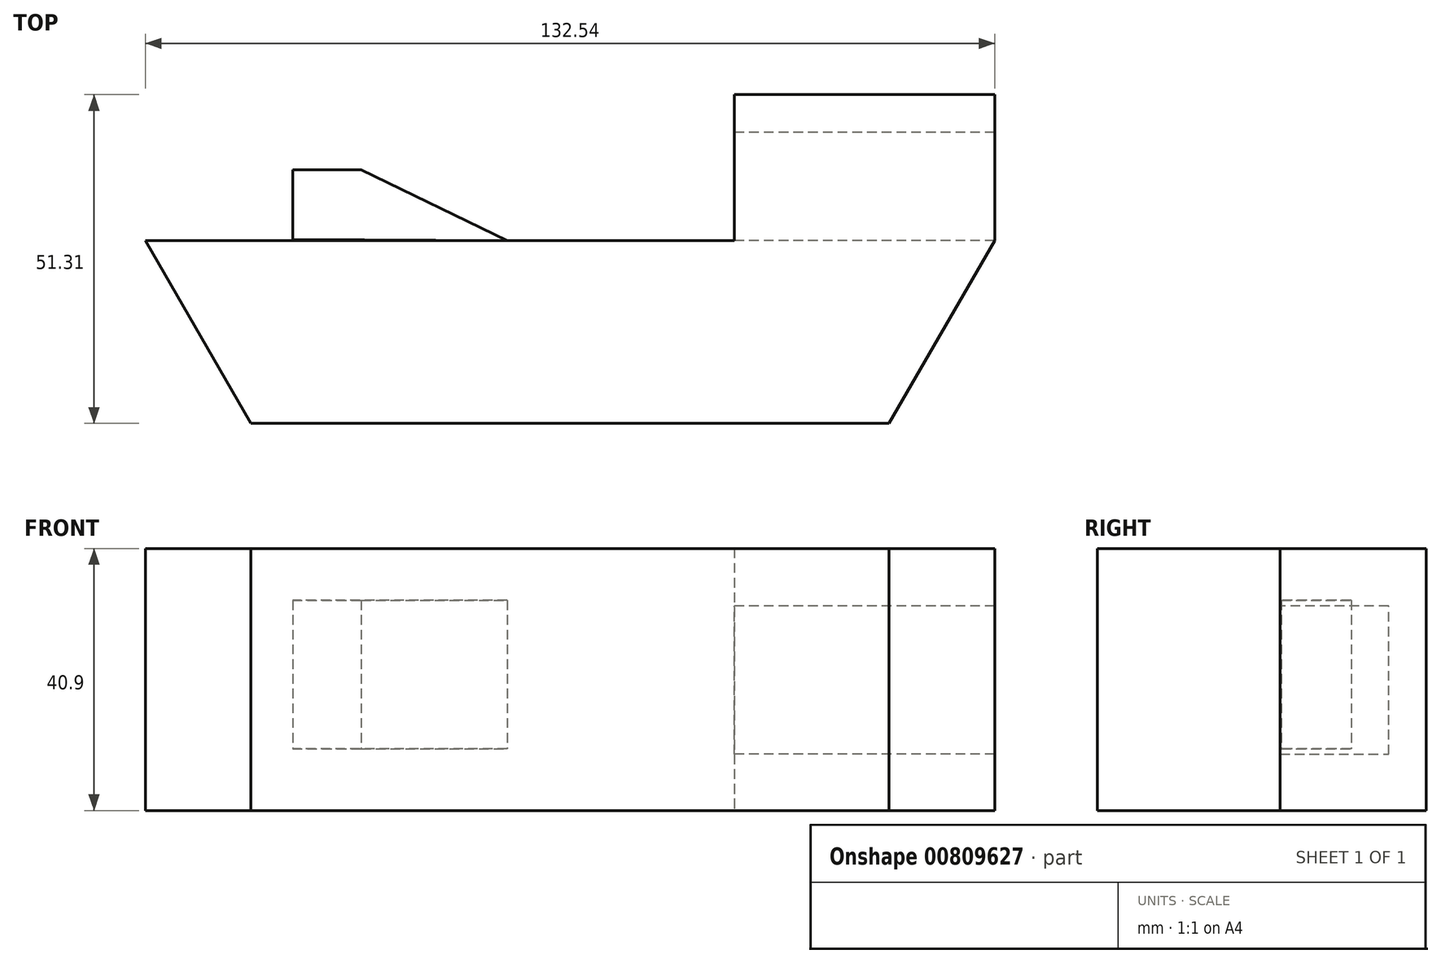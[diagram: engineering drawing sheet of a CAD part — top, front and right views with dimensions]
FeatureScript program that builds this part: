
annotation { "Feature Type Name" : "Feature", "Feature Type Description" : "" }
export const myFeature = defineFeature(function(context is Context, id is Id, definition is map)
    precondition{}
    {
        {
            var Q0;
            Q0=qCreatedBy(makeId("Top.planeOp"),FACE);
            var sketch = newSketch(context, id + "F0", { "sketchPlane" : qUnion([Q0])});
            skLineSegment(sketch, "E0.bottom", {"start": v(-66.27, 14.26) * mm, "end": v(66.27, 14.26) * mm});
            skLineSegment(sketch, "E0.top", {"start": v(-49.8, -14.26) * mm, "end": v(49.8, -14.26) * mm});
            skPoint(sketch, "E0.middle", {"position": v(0, 0) * mm});
            skLineSegment(sketch, "E1", {"start": v(-66.27, 14.26) * mm, "end": v(-49.8, -14.26) * mm});
            skLineSegment(sketch, "E2", {"start": v(66.27, 14.26) * mm, "end": v(49.8, -14.26) * mm});
            skPoint(sketch, "E3.orphan", {"position": v(-66.27, -14.26) * mm});
            skPoint(sketch, "E4.orphan", {"position": v(66.27, -14.26) * mm});
            skLineSegment(sketch, "E5", {"start": v(66.27, 14.26) * mm, "end": v(66.27, 37.05) * mm});
            skLineSegment(sketch, "E6", {"start": v(66.27, 37.05) * mm, "end": v(25.66, 37.05) * mm});
            skLineSegment(sketch, "E7", {"start": v(25.66, 37.05) * mm, "end": v(25.66, 14.26) * mm});
            skLineSegment(sketch, "E8", {"start": v(25.66, 14.26) * mm, "end": v(66.27, 14.26) * mm});
            skSolve(sketch);
        }
        {
            var Q0;
            Q0 = qSketchRegion(id + "F0", true);
            extrude(context, id + "F1", {"entities" : qUnion([Q0]), "depth" : 40.9 * mm, "offsetDistance" : 25 * mm});
        }
        {
            var Q0;
            Q0=qCreatedBy(makeId("Top.planeOp"),FACE);
            cPlane(context, id + "F2", {"entities" : qUnion([Q0]), "cplaneType" : CPlaneType.OFFSET, "offset" : 21.2 * mm, "width" : 150 * mm, "height" : 150 * mm});
        }
        {
            var Q0;
            Q0=qCreatedBy(id+"F2.planeOp",FACE);
            var sketch = newSketch(context, id + "F3", { "sketchPlane" : qUnion([Q0])});
            skLineSegment(sketch, "E9", {"start": v(-43.29, 14.46) * mm, "end": v(-43.29, 25.36) * mm});
            skLineSegment(sketch, "E10", {"start": v(-43.29, 25.36) * mm, "end": v(-32.59, 25.36) * mm});
            skLineSegment(sketch, "E11", {"start": v(-32.59, 25.36) * mm, "end": v(-9.8, 14.26) * mm});
            skLineSegment(sketch, "E12", {"start": v(-9.8, 14.26) * mm, "end": v(-43.29, 14.46) * mm});
            skSolve(sketch);
        }
        {
            var Q0;
            Q0=makeQuery(id+"F3.imprint","IMPRINT",FACE,{"disambiguationData":[TD([[makeQuery(id+"F3.imprint","IMPRINT",EDGE,{"derivedFrom":sQuery(id+"F3.wireOp",EDGE,"E9")}),-1.0]])]});
            extrude(context, id + "F4", {"entities" : qUnion([Q0]), "endBound" : BoundingType.SYMMETRIC, "depth" : 23.2 * mm, "offsetDistance" : 25 * mm});
        }
        {
            var Q0;
            Q0=makeQuery(id+"F1.opExtrude","SWEPT_FACE",FACE,{"disambiguationData":[OSD([sQuery(id+"F0.wireOp",EDGE,"E7")])]});
            var sketch = newSketch(context, id + "F5", { "sketchPlane" : qUnion([Q0])});
            skLineSegment(sketch, "E13", {"start": v(-14.26, 8.78) * mm, "end": v(-31.19, 8.78) * mm});
            skLineSegment(sketch, "E14", {"start": v(-31.19, 8.78) * mm, "end": v(-31.19, 31.89) * mm});
            skLineSegment(sketch, "E15", {"start": v(-31.19, 31.89) * mm, "end": v(-14.26, 31.89) * mm});
            skSolve(sketch);
        }
        {
            var Q0;
            Q0 = qSketchRegion(id + "F5", true);
            var Q1;
            {var subQ0=sQuery(id+"F5.wireOp",EDGE,"E13");Q1=makeQuery(id+"F5.imprint","IMPRINT",FACE,{"disambiguationData":[TD([[makeQuery(id+"F5.imprint","IMPRINT",EDGE,{"derivedFrom":subQ0}),-1.0]])]});}
            extrude(context, id + "F6", {"entities" : qUnion([Q0, Q1]), "operationType" : NewBodyOperationType.REMOVE, "oppositeDirection" : true, "depth" : 40.6 * mm, "offsetDistance" : 25 * mm});
        }
    });
